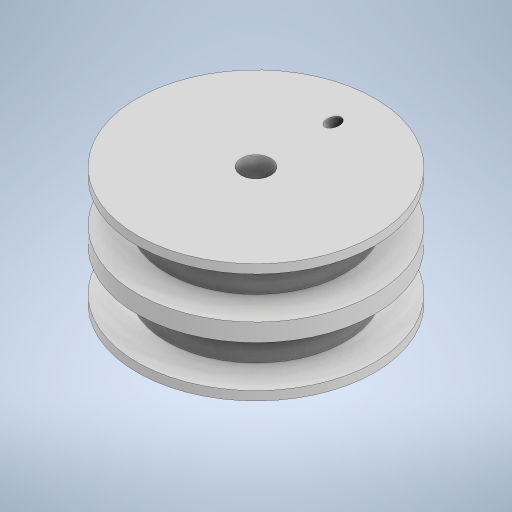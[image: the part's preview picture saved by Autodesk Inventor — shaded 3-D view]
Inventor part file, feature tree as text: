
AUTODESK INVENTOR PART (.ipt)
format: ipt  version: 2023.1 (Build 271208000, 208)  size: 325,632 bytes
history: native  units: mm
features: sketch x7, extrude x4, revolve x2, other x1, mirror x1, fillet x1
ambient origin geometry x8: Origin, YZ Plane, XZ Plane, XY Plane, X Axis, Y Axis, Z Axis, Center Point
bodies: Body1 (feature_tree)
feature tree (16):
  other  "솔리드1"
  extrude  "돌출1"  Depth=9.0mm
  extrude  "돌출2"  Depth=5.8mm
  extrude  "돌출3"  Depth=0.5mm
  sketch  "스케치4"
  revolve  "회전1"
  revolve  "회전2"
  mirror  "미러1"
  extrude  "돌출4"  Depth=6.0mm TaperAngle=0.0deg
  fillet  "모깎기1"  Radius=1.0mm
  sketch  "스케치1"
  sketch  "스케치2"
  sketch  "스케치3"
  sketch  "스케치5"
  sketch  "스케치6"
  sketch  "스케치7"
